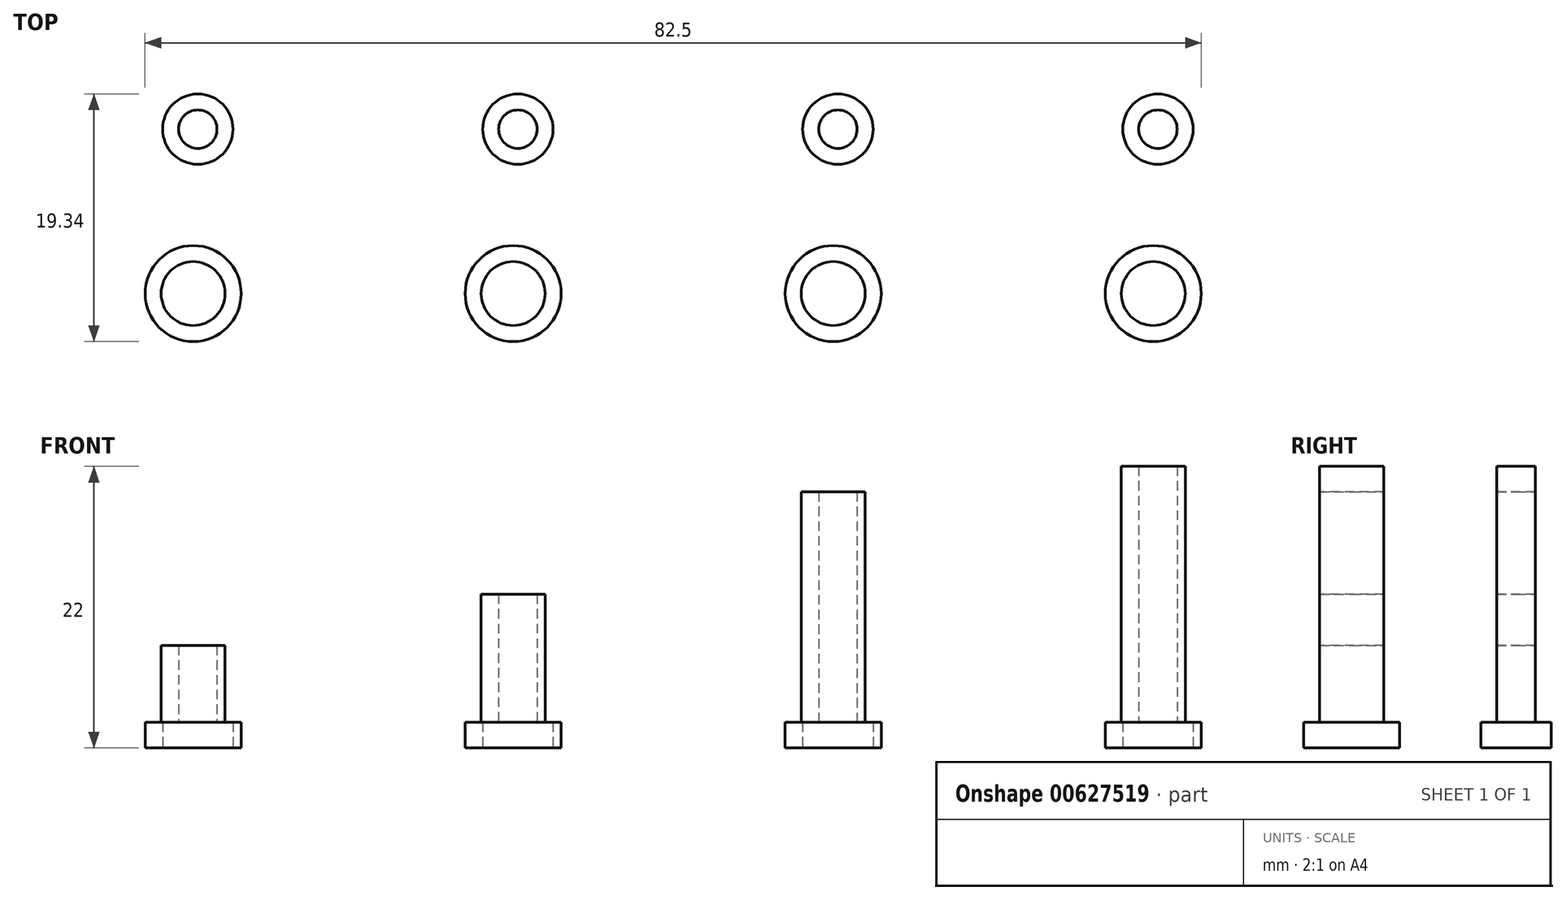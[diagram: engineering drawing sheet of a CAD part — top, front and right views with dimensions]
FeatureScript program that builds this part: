
annotation { "Feature Type Name" : "Feature", "Feature Type Description" : "" }
export const myFeature = defineFeature(function(context is Context, id is Id, definition is map)
    precondition{}
    {
        {
            var Q0;
            Q0=qCreatedBy(makeId("Top.planeOp"),FACE);
            var sketch = newSketch(context, id + "F0", { "sketchPlane" : qUnion([Q0])});
            skCircle(sketch, "E0", {"center": v(-22, 9.85) * mm, "radius": 2.75 * mm});
            skCircle(sketch, "E1", {"center": v(-22.38, -3) * mm, "radius": 3.75 * mm});
            skCircle(sketch, "E2.1.0.0", {"center": v(3, 9.85) * mm, "radius": 2.75 * mm});
            skCircle(sketch, "E2.1.0.1", {"center": v(2.62, -3) * mm, "radius": 3.75 * mm});
            skCircle(sketch, "E2.2.0.0", {"center": v(28, 9.85) * mm, "radius": 2.75 * mm});
            skCircle(sketch, "E2.2.0.1", {"center": v(27.62, -3) * mm, "radius": 3.75 * mm});
            skCircle(sketch, "E2.3.0.0", {"center": v(53, 9.85) * mm, "radius": 2.75 * mm});
            skCircle(sketch, "E2.3.0.1", {"center": v(52.62, -3) * mm, "radius": 3.75 * mm});
            skLineSegment(sketch, "E2.direction1", {"start": v(-22, 9.85) * mm, "end": v(3, 9.85) * mm, "construction": true});
            skSolve(sketch);
        }
        {
            var Q0;
            Q0=makeQuery(id+"F0.imprint","IMPRINT",FACE,{"disambiguationData":[TD([[makeQuery(id+"F0.imprint","IMPRINT",EDGE,{"derivedFrom":sQuery(id+"F0.wireOp",EDGE,"E0")}),1.0]])]});
            var Q1;
            Q1=makeQuery(id+"F0.imprint","IMPRINT",FACE,{"disambiguationData":[TD([[makeQuery(id+"F0.imprint","IMPRINT",EDGE,{"derivedFrom":sQuery(id+"F0.wireOp",EDGE,"E2.1.0.0")}),1.0]])]});
            var Q2;
            Q2=makeQuery(id+"F0.imprint","IMPRINT",FACE,{"disambiguationData":[TD([[makeQuery(id+"F0.imprint","IMPRINT",EDGE,{"derivedFrom":sQuery(id+"F0.wireOp",EDGE,"E2.2.0.0")}),1.0]])]});
            var Q3;
            Q3=makeQuery(id+"F0.imprint","IMPRINT",FACE,{"disambiguationData":[TD([[makeQuery(id+"F0.imprint","IMPRINT",EDGE,{"derivedFrom":sQuery(id+"F0.wireOp",EDGE,"E1")}),1.0]])]});
            var Q4;
            Q4=makeQuery(id+"F0.imprint","IMPRINT",FACE,{"disambiguationData":[TD([[makeQuery(id+"F0.imprint","IMPRINT",EDGE,{"derivedFrom":sQuery(id+"F0.wireOp",EDGE,"E2.2.0.1")}),1.0]])]});
            var Q5;
            Q5=makeQuery(id+"F0.imprint","IMPRINT",FACE,{"disambiguationData":[TD([[makeQuery(id+"F0.imprint","IMPRINT",EDGE,{"derivedFrom":sQuery(id+"F0.wireOp",EDGE,"E2.3.0.0")}),1.0]])]});
            var Q6;
            Q6=makeQuery(id+"F0.imprint","IMPRINT",FACE,{"disambiguationData":[TD([[makeQuery(id+"F0.imprint","IMPRINT",EDGE,{"derivedFrom":sQuery(id+"F0.wireOp",EDGE,"E2.1.0.1")}),1.0]])]});
            var Q7;
            Q7=makeQuery(id+"F0.imprint","IMPRINT",FACE,{"disambiguationData":[TD([[makeQuery(id+"F0.imprint","IMPRINT",EDGE,{"derivedFrom":sQuery(id+"F0.wireOp",EDGE,"E2.3.0.1")}),1.0]])]});
            extrude(context, id + "F1", {"entities" : qUnion([Q0, Q1, Q2, Q3, Q4, Q5, Q6, Q7]), "depth" : 2 * mm, "offsetDistance" : 25 * mm});
        }
        {
            var Q0;
            Q0=makeQuery(id+"F1.opExtrude","CAP_FACE",FACE,{"disambiguationData":[OSD([sQuery(id+"F0.wireOp",EDGE,"E0")])],"isStart":false});
            var sketch = newSketch(context, id + "F2", { "sketchPlane" : qUnion([Q0])});
            skCircle(sketch, "E3", {"center": v(-22, 9.85) * mm, "radius": 1.5 * mm});
            skCircle(sketch, "E4.1.0.0", {"center": v(3, 9.85) * mm, "radius": 1.5 * mm});
            skCircle(sketch, "E4.2.0.0", {"center": v(28, 9.85) * mm, "radius": 1.5 * mm});
            skCircle(sketch, "E4.3.0.0", {"center": v(53, 9.85) * mm, "radius": 1.5 * mm});
            skLineSegment(sketch, "E4.direction1", {"start": v(-22, 9.85) * mm, "end": v(3, 9.85) * mm, "construction": true});
            skSolve(sketch);
        }
        {
            var Q0;
            Q0=makeQuery(id+"F1.opExtrude","CAP_FACE",FACE,{"disambiguationData":[OSD([sQuery(id+"F0.wireOp",EDGE,"E1")])],"isStart":false});
            var sketch = newSketch(context, id + "F3", { "sketchPlane" : qUnion([Q0])});
            skCircle(sketch, "E5", {"center": v(-22.38, -3) * mm, "radius": 2.5 * mm});
            skCircle(sketch, "E6.1.0.0", {"center": v(2.62, -3) * mm, "radius": 2.5 * mm});
            skCircle(sketch, "E6.2.0.0", {"center": v(27.62, -3) * mm, "radius": 2.5 * mm});
            skCircle(sketch, "E6.3.0.0", {"center": v(52.62, -3) * mm, "radius": 2.5 * mm});
            skLineSegment(sketch, "E6.direction1", {"start": v(-22.38, -3) * mm, "end": v(2.62, -3) * mm, "construction": true});
            skSolve(sketch);
        }
        {
            var Q0;
            Q0=makeQuery(id+"F2.imprint","IMPRINT",FACE,{"disambiguationData":[TD([[makeQuery(id+"F2.imprint","IMPRINT",EDGE,{"derivedFrom":sQuery(id+"F2.wireOp",EDGE,"E3")}),1.0]])]});
            var Q1;
            Q1=makeQuery(id+"F3.imprint","IMPRINT",FACE,{"disambiguationData":[TD([[makeQuery(id+"F3.imprint","IMPRINT",EDGE,{"derivedFrom":sQuery(id+"F3.wireOp",EDGE,"E5")}),1.0]])]});
            extrude(context, id + "F4", {"entities" : qUnion([Q0, Q1]), "operationType" : NewBodyOperationType.ADD, "depth" : 6 * mm, "offsetDistance" : 25 * mm});
        }
        {
            var Q0;
            Q0=makeQuery(id+"F3.imprint","IMPRINT",FACE,{"disambiguationData":[TD([[makeQuery(id+"F3.imprint","IMPRINT",EDGE,{"derivedFrom":sQuery(id+"F3.wireOp",EDGE,"E6.1.0.0")}),1.0]])]});
            var Q1;
            Q1=makeQuery(id+"F2.imprint","IMPRINT",FACE,{"disambiguationData":[TD([[makeQuery(id+"F2.imprint","IMPRINT",EDGE,{"derivedFrom":sQuery(id+"F2.wireOp",EDGE,"E4.1.0.0")}),1.0]])]});
            extrude(context, id + "F5", {"entities" : qUnion([Q0, Q1]), "operationType" : NewBodyOperationType.ADD, "depth" : 10 * mm, "offsetDistance" : 25 * mm});
        }
        {
            var Q0;
            Q0=makeQuery(id+"F2.imprint","IMPRINT",FACE,{"disambiguationData":[TD([[makeQuery(id+"F2.imprint","IMPRINT",EDGE,{"derivedFrom":sQuery(id+"F2.wireOp",EDGE,"E4.2.0.0")}),1.0]])]});
            var Q1;
            Q1=makeQuery(id+"F3.imprint","IMPRINT",FACE,{"disambiguationData":[TD([[makeQuery(id+"F3.imprint","IMPRINT",EDGE,{"derivedFrom":sQuery(id+"F3.wireOp",EDGE,"E6.2.0.0")}),1.0]])]});
            extrude(context, id + "F6", {"entities" : qUnion([Q0, Q1]), "operationType" : NewBodyOperationType.ADD, "depth" : 18 * mm, "offsetDistance" : 25 * mm});
        }
        {
            var Q0;
            Q0=makeQuery(id+"F2.imprint","IMPRINT",FACE,{"disambiguationData":[TD([[makeQuery(id+"F2.imprint","IMPRINT",EDGE,{"derivedFrom":sQuery(id+"F2.wireOp",EDGE,"E4.3.0.0")}),1.0]])]});
            var Q1;
            Q1=makeQuery(id+"F3.imprint","IMPRINT",FACE,{"disambiguationData":[TD([[makeQuery(id+"F3.imprint","IMPRINT",EDGE,{"derivedFrom":sQuery(id+"F3.wireOp",EDGE,"E6.3.0.0")}),1.0]])]});
            extrude(context, id + "F7", {"entities" : qUnion([Q0, Q1]), "operationType" : NewBodyOperationType.ADD, "depth" : 20 * mm, "offsetDistance" : 25 * mm});
        }
    });
